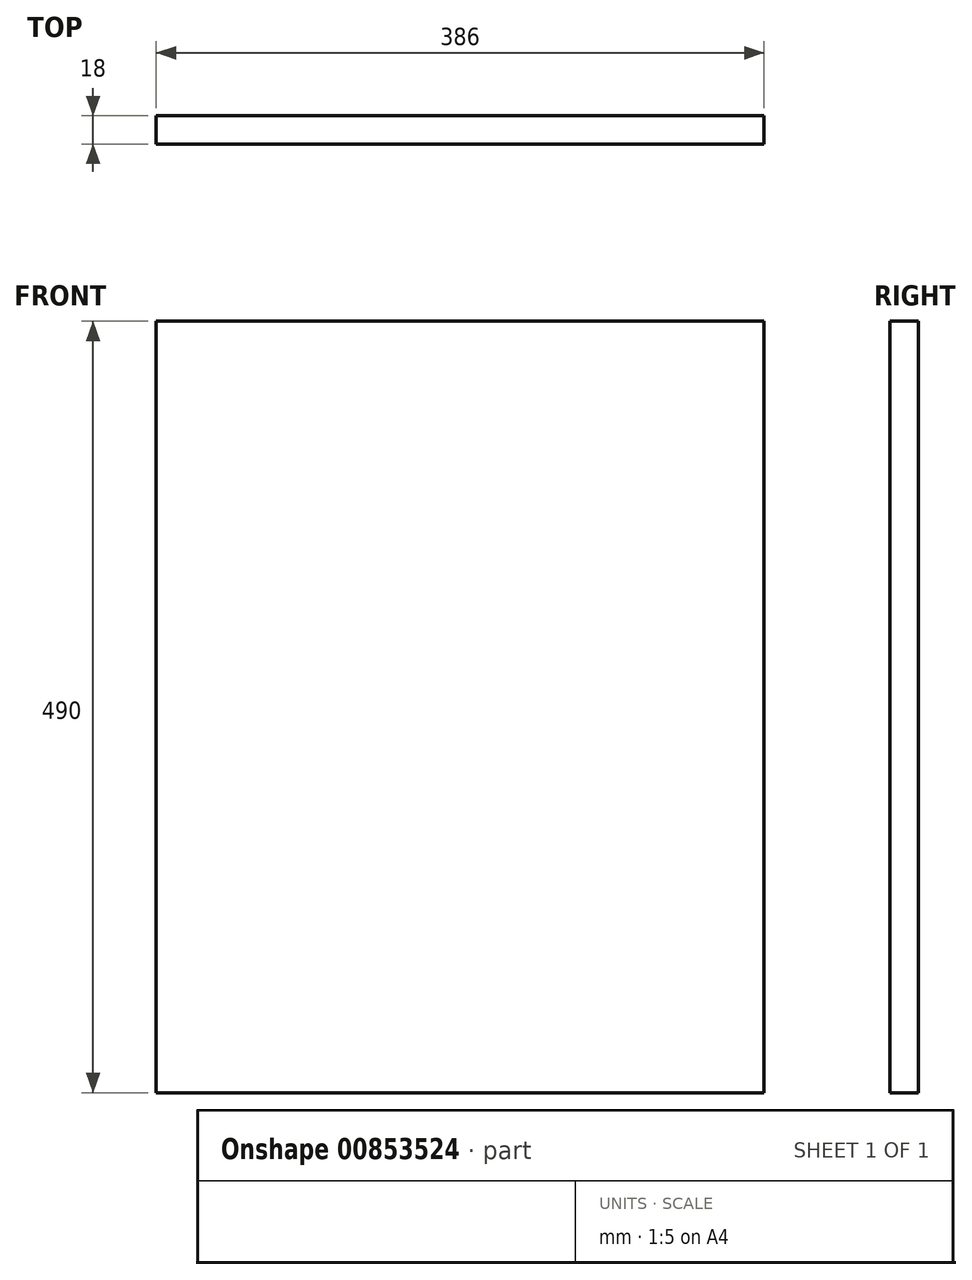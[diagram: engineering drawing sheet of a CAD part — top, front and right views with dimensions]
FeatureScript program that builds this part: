
annotation { "Feature Type Name" : "Feature", "Feature Type Description" : "" }
export const myFeature = defineFeature(function(context is Context, id is Id, definition is map)
    precondition{}
    {
        {
            var Q0;
            Q0=qCreatedBy(makeId("Front.planeOp"),FACE);
            var sketch = newSketch(context, id + "F0", { "sketchPlane" : qUnion([Q0])});
            skLineSegment(sketch, "E0.bottom", {"start": v(193, 245) * mm, "end": v(-193, 245) * mm});
            skLineSegment(sketch, "E0.top", {"start": v(193, -245) * mm, "end": v(-193, -245) * mm});
            skLineSegment(sketch, "E0.left", {"start": v(193, 245) * mm, "end": v(193, -245) * mm});
            skLineSegment(sketch, "E0.right", {"start": v(-193, 245) * mm, "end": v(-193, -245) * mm});
            skPoint(sketch, "E0.middle", {"position": v(0, 0) * mm});
            skSolve(sketch);
        }
        {
            var Q0;
            Q0 = qSketchRegion(id + "F0", true);
            extrude(context, id + "F1", {"entities" : qUnion([Q0]), "depth" : 18 * mm, "offsetDistance" : 25 * mm});
        }
    });
